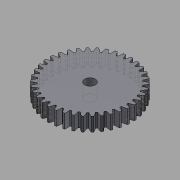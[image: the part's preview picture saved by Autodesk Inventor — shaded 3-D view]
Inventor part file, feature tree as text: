
AUTODESK INVENTOR PART (.ipt)
format: ipt  version: 2015 (Build 190159000, 159)  size: 339,968 bytes
history: native  units: in
note: dims shown in document units (in); Inventor stores cm internally (conversion verified against a paired STEP export)
features: other x13, sketch x3, plane x2
ambient origin geometry x8: Origin, YZ Plane, XZ Plane, XY Plane, X Axis, Y Axis, Z Axis, Center Point
bodies: Solid1 (feature_tree)
feature tree (18):
  other  "Spur Gear24_MIR3.ipt"
  other  "Solid1::Spur Gear24_MIR3.ipt"
  other  "TaggingFeature1"
  sketch  "Sketch1"  dims[d0=0.3937in]
  sketch  "Sketch2"  dims[d16=0.4724in d17=0.0in d41=0.0in d43=0.4724in d46=0.4724in d47=0.0in d48=0.0in]
  sketch  "Sketch3"
  plane  "XZ Plane_1"
  plane  "Work Plane2"
  other  "Z Axis_1"
  other  "Srf1"
  other  "Srf1::Derived"
  other  "Distance iMate"
  other  "Align iMate"
  other  "Mesh iMate"
  other  "Axis iMate"
  other  "Position iMate"
  other  "Mesh iMate2"
  other  "Start plane iMate"
